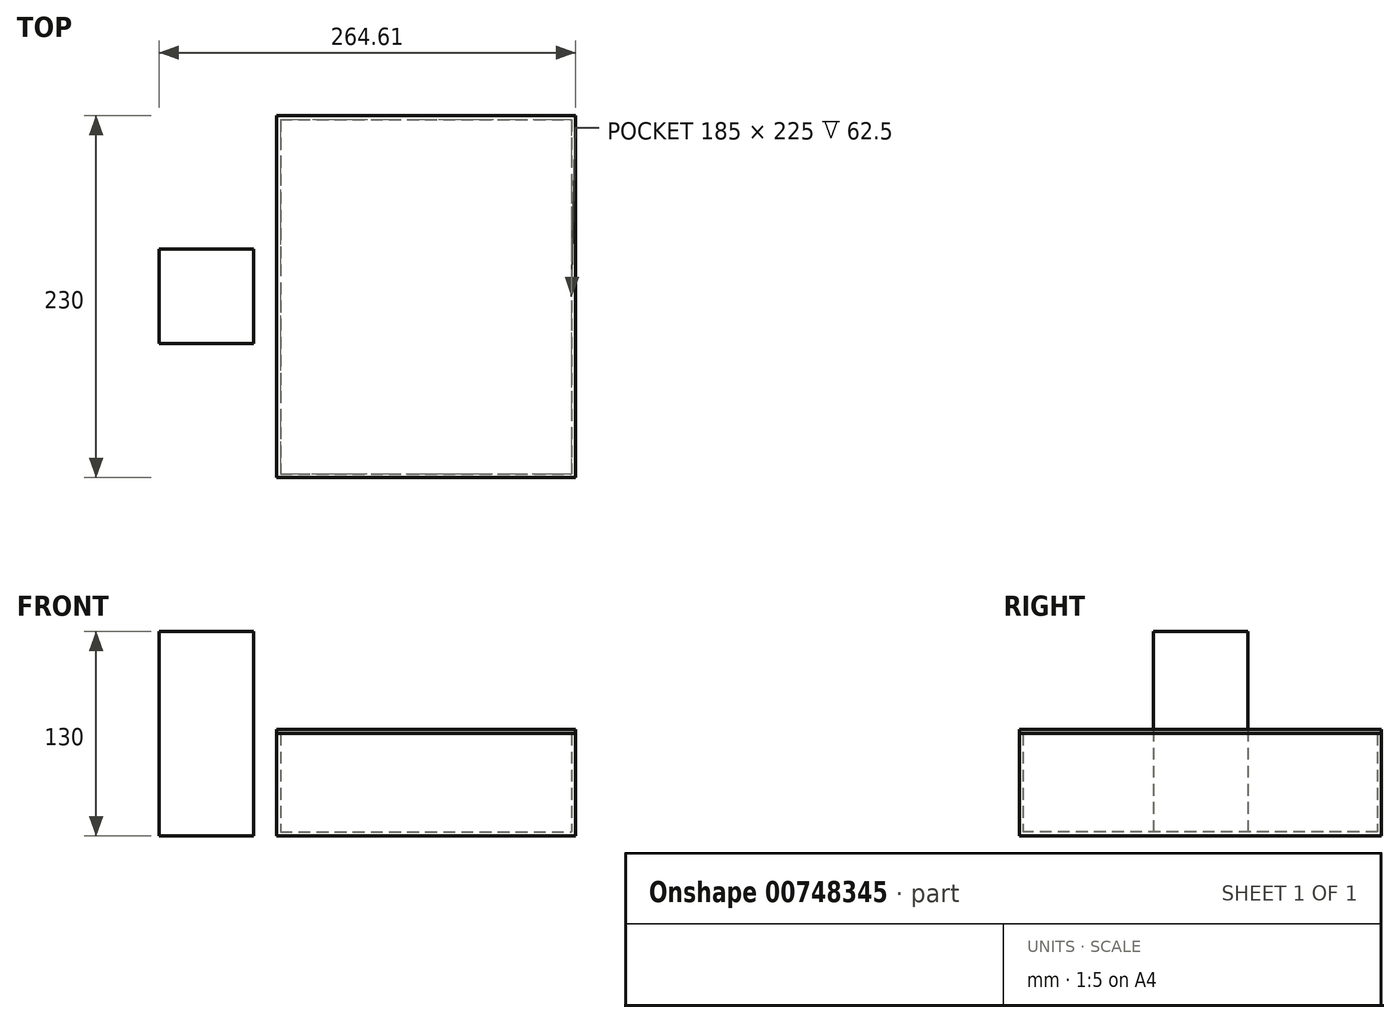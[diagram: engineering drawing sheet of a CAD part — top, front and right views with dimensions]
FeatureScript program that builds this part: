
annotation { "Feature Type Name" : "Feature", "Feature Type Description" : "" }
export const myFeature = defineFeature(function(context is Context, id is Id, definition is map)
    precondition{}
    {
        {
            var Q0;
            Q0=qCreatedBy(makeId("Top.planeOp"),FACE);
            var sketch = newSketch(context, id + "F0", { "sketchPlane" : qUnion([Q0])});
            skLineSegment(sketch, "E0.bottom", {"start": v(-75.64, 116.86) * mm, "end": v(114.36, 116.86) * mm});
            skLineSegment(sketch, "E0.top", {"start": v(-75.64, -113.14) * mm, "end": v(114.36, -113.14) * mm});
            skLineSegment(sketch, "E0.left", {"start": v(-75.64, 116.86) * mm, "end": v(-75.64, -113.14) * mm});
            skLineSegment(sketch, "E0.right", {"start": v(114.36, 116.86) * mm, "end": v(114.36, -113.14) * mm});
            skSolve(sketch);
        }
        {
            var Q0;
            Q0=makeQuery(id+"F0.imprint","IMPRINT",FACE,{"disambiguationData":[TD([[makeQuery(id+"F0.imprint","IMPRINT",EDGE,{"derivedFrom":sQuery(id+"F0.wireOp",EDGE,"E0.bottom")}),-1.0]])]});
            extrude(context, id + "F1", {"entities" : qUnion([Q0]), "depth" : 65 * mm, "offsetDistance" : 25 * mm});
        }
        {
            var Q0;
            Q0=makeQuery(id+"F1.opExtrude","CAP_FACE",FACE,{"disambiguationData":[OSD([sQuery(id+"F0.wireOp",EDGE,"E0.bottom"),sQuery(id+"F0.wireOp",EDGE,"E0.top"),sQuery(id+"F0.wireOp",EDGE,"E0.left"),sQuery(id+"F0.wireOp",EDGE,"E0.right")])],"isStart":false});
            shell(context, id + "F2", {"entities" : qUnion([Q0]), "thickness" : 2.5 * mm});
        }
        {
            var Q0;
            Q0=makeQuery(id+"F1.opExtrude","CAP_FACE",FACE,{"disambiguationData":[OSD([sQuery(id+"F0.wireOp",EDGE,"E0.bottom"),sQuery(id+"F0.wireOp",EDGE,"E0.top"),sQuery(id+"F0.wireOp",EDGE,"E0.left"),sQuery(id+"F0.wireOp",EDGE,"E0.right")])],"isStart":false});
            var sketch = newSketch(context, id + "F3", { "sketchPlane" : qUnion([Q0])});
            skLineSegment(sketch, "E1.0", {"start": v(-75.64, 116.86) * mm, "end": v(114.36, 116.86) * mm});
            skLineSegment(sketch, "E2.0", {"start": v(-75.64, -113.14) * mm, "end": v(114.36, -113.14) * mm});
            skLineSegment(sketch, "E3.left", {"start": v(-75.64, 116.86) * mm, "end": v(-75.64, -113.14) * mm});
            skLineSegment(sketch, "E3.right", {"start": v(114.36, 116.86) * mm, "end": v(114.36, -113.14) * mm});
            skSolve(sketch);
        }
        {
            var Q0;
            Q0 = qSketchRegion(id + "F3", true);
            extrude(context, id + "F4", {"entities" : qUnion([Q0]), "depth" : 2.5 * mm, "offsetDistance" : 25 * mm});
        }
        {
            var Q0;
            Q0=makeQuery(id+"F1.opExtrude","CAP_FACE",FACE,{"disambiguationData":[OSD([sQuery(id+"F0.wireOp",EDGE,"E0.bottom"),sQuery(id+"F0.wireOp",EDGE,"E0.top"),sQuery(id+"F0.wireOp",EDGE,"E0.left"),sQuery(id+"F0.wireOp",EDGE,"E0.right")])],"isStart":true});
            var sketch = newSketch(context, id + "F5", { "sketchPlane" : qUnion([Q0])});
            skLineSegment(sketch, "E4.bottom", {"start": v(-150.25, -32.04) * mm, "end": v(-90.25, -32.04) * mm});
            skLineSegment(sketch, "E4.top", {"start": v(-150.25, 27.96) * mm, "end": v(-90.25, 27.96) * mm});
            skLineSegment(sketch, "E4.left", {"start": v(-150.25, -32.04) * mm, "end": v(-150.25, 27.96) * mm});
            skLineSegment(sketch, "E4.right", {"start": v(-90.25, -32.04) * mm, "end": v(-90.25, 27.96) * mm});
            skSolve(sketch);
        }
        {
            var Q0;
            Q0 = qSketchRegion(id + "F5", true);
            extrude(context, id + "F6", {"entities" : qUnion([Q0]), "depth" : 0 * mm, "offsetDistance" : 25 * mm, "hasSecondDirection" : true, "secondDirectionOppositeDirection" : true, "secondDirectionDepth" : 130 * mm});
        }
    });
